# Revit family: Human_Solution-UPLIFT_Desk_LAMP_CLAMP_MOUNT_LTG001
name_source: partatom
category: Lighting Fixtures
units: mm (PartAtom-declared; Revit-internal decimal feet)

## family parameters
Always vertical = Yes
Cut with Voids When Loaded = No
Light Source = No
OmniClass Number = 23.40.20.00
OmniClass Title = General Furniture and Specialties
Part Type = Normal
Room Calculation Point = No
Round Connector Dimension = Use Diameter
Shared = No
Work Plane-Based = No

## types (1)
- E7 LED Desk Lamp
    Assembly Code = E2020200
    Depth = 1 1/2"
    Description = E7 LED Desk Lamp  13.5"W 1 11/16"D 22.5"H
    Height = 22 1/2"
    Keynote = 12500
    Low Emitting Finish = Yes
    Low Emitting Material = Yes
    Manufacturer = Human Solution
    Model = LTG001- LAMP WITH CLAMP MOUNT
    Percentage of Recycled Content = 0
    Salvage or Reuse = Yes
    Type Comments = Lighting
    URL = https://www.thehumansolution.com
    Unit = HMS - Aluminum
    Voltage = 120 V
    Width = 13 1/2"

## geometry (parser evidence)
native form markers: Sweep x2
no freeform markers — native parametric forms only
